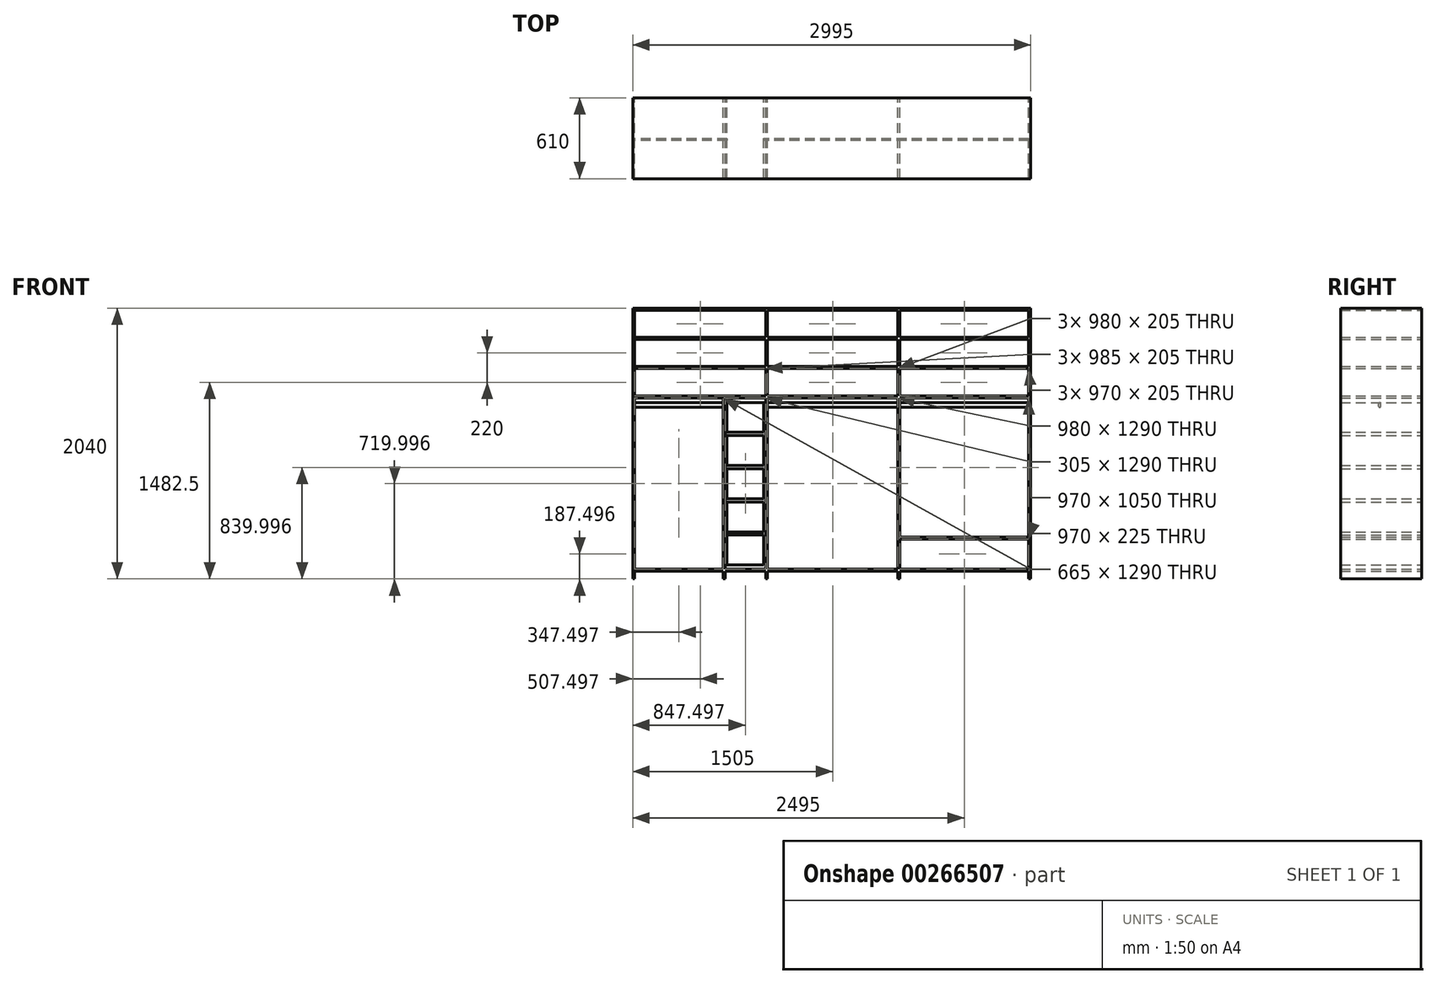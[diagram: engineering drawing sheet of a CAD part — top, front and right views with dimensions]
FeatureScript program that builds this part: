
annotation { "Feature Type Name" : "Feature", "Feature Type Description" : "" }
export const myFeature = defineFeature(function(context is Context, id is Id, definition is map)
    precondition{}
    {
        {
            var Q0;
            Q0=qCreatedBy(makeId("Front.planeOp"),FACE);
            var sketch = newSketch(context, id + "F0", { "sketchPlane" : qUnion([Q0])});
            skLineSegment(sketch, "E0.bottom", {"start": v(253.93, 1797.17) * mm, "end": v(268.93, 1797.17) * mm});
            skLineSegment(sketch, "E0.top", {"start": v(253.93, -242.83) * mm, "end": v(268.93, -242.83) * mm});
            skLineSegment(sketch, "E0.left", {"start": v(253.93, 1797.17) * mm, "end": v(253.93, -242.83) * mm});
            skLineSegment(sketch, "E0.right", {"start": v(268.93, 1797.17) * mm, "end": v(268.93, -242.83) * mm});
            skLineSegment(sketch, "E1.bottom", {"start": v(268.93, -182.83) * mm, "end": v(933.93, -182.83) * mm});
            skLineSegment(sketch, "E1.top", {"start": v(268.93, -167.83) * mm, "end": v(933.93, -167.83) * mm});
            skLineSegment(sketch, "E1.left", {"start": v(268.93, -182.83) * mm, "end": v(268.93, -167.83) * mm});
            skLineSegment(sketch, "E1.right", {"start": v(933.93, -182.83) * mm, "end": v(933.93, -167.83) * mm});
            skLineSegment(sketch, "E2.bottom", {"start": v(1268.93, -242.83) * mm, "end": v(1253.93, -242.83) * mm});
            skLineSegment(sketch, "E2.top", {"start": v(1268.93, 1797.17) * mm, "end": v(1253.93, 1797.17) * mm});
            skLineSegment(sketch, "E2.left", {"start": v(1268.93, -242.83) * mm, "end": v(1268.93, 1797.17) * mm});
            skLineSegment(sketch, "E2.right", {"start": v(1253.93, -242.83) * mm, "end": v(1253.93, 1797.17) * mm});
            skLineSegment(sketch, "E3.bottom", {"start": v(268.93, 1797.17) * mm, "end": v(1253.93, 1797.17) * mm});
            skLineSegment(sketch, "E3.top", {"start": v(268.93, 1782.17) * mm, "end": v(1253.93, 1782.17) * mm});
            skLineSegment(sketch, "E3.left", {"start": v(268.93, 1797.17) * mm, "end": v(268.93, 1782.17) * mm});
            skLineSegment(sketch, "E3.right", {"start": v(1253.93, 1797.17) * mm, "end": v(1253.93, 1782.17) * mm});
            skLineSegment(sketch, "E4.bottom", {"start": v(268.93, 1577.17) * mm, "end": v(1253.93, 1577.17) * mm});
            skLineSegment(sketch, "E4.top", {"start": v(268.93, 1562.17) * mm, "end": v(1253.93, 1562.17) * mm});
            skLineSegment(sketch, "E4.left", {"start": v(268.93, 1577.17) * mm, "end": v(268.93, 1562.17) * mm});
            skLineSegment(sketch, "E4.right", {"start": v(1253.93, 1577.17) * mm, "end": v(1253.93, 1562.17) * mm});
            skLineSegment(sketch, "E5.bottom", {"start": v(268.93, 1357.17) * mm, "end": v(1253.93, 1357.17) * mm});
            skLineSegment(sketch, "E5.top", {"start": v(268.93, 1342.17) * mm, "end": v(1253.93, 1342.17) * mm});
            skLineSegment(sketch, "E5.left", {"start": v(268.93, 1357.17) * mm, "end": v(268.93, 1342.17) * mm});
            skLineSegment(sketch, "E5.right", {"start": v(1253.93, 1357.17) * mm, "end": v(1253.93, 1342.17) * mm});
            skLineSegment(sketch, "E6.bottom", {"start": v(268.93, 1137.17) * mm, "end": v(1253.93, 1137.17) * mm});
            skLineSegment(sketch, "E6.top", {"start": v(268.93, 1122.17) * mm, "end": v(1253.93, 1122.17) * mm});
            skLineSegment(sketch, "E6.left", {"start": v(268.93, 1137.17) * mm, "end": v(268.93, 1122.17) * mm});
            skLineSegment(sketch, "E6.right", {"start": v(1253.93, 1137.17) * mm, "end": v(1253.93, 1122.17) * mm});
            skLineSegment(sketch, "E7.bottom", {"start": v(933.93, -242.83) * mm, "end": v(948.93, -242.83) * mm});
            skLineSegment(sketch, "E7.top", {"start": v(933.93, 1122.17) * mm, "end": v(948.93, 1122.17) * mm});
            skLineSegment(sketch, "E7.left", {"start": v(933.93, -242.83) * mm, "end": v(933.93, 1122.17) * mm});
            skLineSegment(sketch, "E7.right", {"start": v(948.93, -242.83) * mm, "end": v(948.93, 1122.17) * mm});
            skLineSegment(sketch, "E8.bottom", {"start": v(948.93, -167.83) * mm, "end": v(1253.93, -167.83) * mm});
            skLineSegment(sketch, "E8.top", {"start": v(948.93, -182.83) * mm, "end": v(1253.93, -182.83) * mm});
            skLineSegment(sketch, "E8.left", {"start": v(948.93, -167.83) * mm, "end": v(948.93, -182.83) * mm});
            skLineSegment(sketch, "E8.right", {"start": v(1253.93, -167.83) * mm, "end": v(1253.93, -182.83) * mm});
            skLineSegment(sketch, "E9.bottom", {"start": v(1238.93, 862.17) * mm, "end": v(963.93, 862.17) * mm});
            skLineSegment(sketch, "E9.top", {"start": v(1238.93, 1087.17) * mm, "end": v(963.93, 1087.17) * mm});
            skLineSegment(sketch, "E9.left", {"start": v(1238.93, 862.17) * mm, "end": v(1238.93, 1087.17) * mm});
            skLineSegment(sketch, "E9.right", {"start": v(963.93, 862.17) * mm, "end": v(963.93, 1087.17) * mm});
            skLineSegment(sketch, "E10", {"start": v(963.93, 862.17) * mm, "end": v(963.93, 660.08) * mm, "construction": true});
            skLineSegment(sketch, "E11.1.0.0", {"start": v(1238.93, 612.17) * mm, "end": v(1238.93, 837.17) * mm});
            skLineSegment(sketch, "E11.1.0.1", {"start": v(963.93, 612.17) * mm, "end": v(963.93, 837.17) * mm});
            skLineSegment(sketch, "E11.1.0.2", {"start": v(1238.93, 612.17) * mm, "end": v(963.93, 612.17) * mm});
            skLineSegment(sketch, "E11.1.0.3", {"start": v(1238.93, 837.17) * mm, "end": v(963.93, 837.17) * mm});
            skLineSegment(sketch, "E11.2.0.0", {"start": v(1238.93, 362.17) * mm, "end": v(1238.93, 587.17) * mm});
            skLineSegment(sketch, "E11.2.0.1", {"start": v(963.93, 362.17) * mm, "end": v(963.93, 587.17) * mm});
            skLineSegment(sketch, "E11.2.0.2", {"start": v(1238.93, 362.17) * mm, "end": v(963.93, 362.17) * mm});
            skLineSegment(sketch, "E11.2.0.3", {"start": v(1238.93, 587.17) * mm, "end": v(963.93, 587.17) * mm});
            skLineSegment(sketch, "E11.direction1", {"start": v(963.93, 862.17) * mm, "end": v(963.93, 612.17) * mm, "construction": true});
            skLineSegment(sketch, "E12.0.3.0", {"start": v(1238.93, 112.17) * mm, "end": v(1238.93, 337.17) * mm});
            skLineSegment(sketch, "E12.3.3.0", {"start": v(963.93, 112.17) * mm, "end": v(963.93, 337.17) * mm});
            skLineSegment(sketch, "E12.6.3.0", {"start": v(1238.93, 112.17) * mm, "end": v(963.93, 112.17) * mm});
            skLineSegment(sketch, "E12.9.3.0", {"start": v(1238.93, 337.17) * mm, "end": v(963.93, 337.17) * mm});
            skLineSegment(sketch, "E12.0.4.0", {"start": v(1238.93, -137.83) * mm, "end": v(1238.93, 87.17) * mm});
            skLineSegment(sketch, "E12.3.4.0", {"start": v(963.93, -137.83) * mm, "end": v(963.93, 87.17) * mm});
            skLineSegment(sketch, "E12.6.4.0", {"start": v(1238.93, -137.83) * mm, "end": v(963.93, -137.83) * mm});
            skLineSegment(sketch, "E12.9.4.0", {"start": v(1238.93, 87.17) * mm, "end": v(963.93, 87.17) * mm});
            skLineSegment(sketch, "E13.bottom", {"start": v(2248.93, 1797.17) * mm, "end": v(2263.93, 1797.17) * mm});
            skLineSegment(sketch, "E13.top", {"start": v(2248.93, -242.83) * mm, "end": v(2263.93, -242.83) * mm});
            skLineSegment(sketch, "E13.left", {"start": v(2248.93, 1797.17) * mm, "end": v(2248.93, -242.83) * mm});
            skLineSegment(sketch, "E13.right", {"start": v(2263.93, 1797.17) * mm, "end": v(2263.93, -242.83) * mm});
            skLineSegment(sketch, "E14.bottom", {"start": v(1268.93, -167.83) * mm, "end": v(2248.93, -167.83) * mm});
            skLineSegment(sketch, "E14.top", {"start": v(1268.93, -182.83) * mm, "end": v(2248.93, -182.83) * mm});
            skLineSegment(sketch, "E14.left", {"start": v(1268.93, -167.83) * mm, "end": v(1268.93, -182.83) * mm});
            skLineSegment(sketch, "E14.right", {"start": v(2248.93, -167.83) * mm, "end": v(2248.93, -182.83) * mm});
            skLineSegment(sketch, "E15.bottom", {"start": v(1268.93, 1122.17) * mm, "end": v(2248.93, 1122.17) * mm});
            skLineSegment(sketch, "E15.top", {"start": v(1268.93, 1137.17) * mm, "end": v(2248.93, 1137.17) * mm});
            skLineSegment(sketch, "E15.left", {"start": v(1268.93, 1122.17) * mm, "end": v(1268.93, 1137.17) * mm});
            skLineSegment(sketch, "E15.right", {"start": v(2248.93, 1122.17) * mm, "end": v(2248.93, 1137.17) * mm});
            skLineSegment(sketch, "E16.bottom", {"start": v(1268.93, 1342.17) * mm, "end": v(2248.93, 1342.17) * mm});
            skLineSegment(sketch, "E16.top", {"start": v(1268.93, 1357.17) * mm, "end": v(2248.93, 1357.17) * mm});
            skLineSegment(sketch, "E16.left", {"start": v(1268.93, 1342.17) * mm, "end": v(1268.93, 1357.17) * mm});
            skLineSegment(sketch, "E16.right", {"start": v(2248.93, 1342.17) * mm, "end": v(2248.93, 1357.17) * mm});
            skLineSegment(sketch, "E17.bottom", {"start": v(1268.93, 1562.17) * mm, "end": v(2248.93, 1562.17) * mm});
            skLineSegment(sketch, "E17.top", {"start": v(1268.93, 1577.17) * mm, "end": v(2248.93, 1577.17) * mm});
            skLineSegment(sketch, "E17.left", {"start": v(1268.93, 1562.17) * mm, "end": v(1268.93, 1577.17) * mm});
            skLineSegment(sketch, "E17.right", {"start": v(2248.93, 1562.17) * mm, "end": v(2248.93, 1577.17) * mm});
            skLineSegment(sketch, "E18.bottom", {"start": v(1268.93, 1782.17) * mm, "end": v(2248.93, 1782.17) * mm});
            skLineSegment(sketch, "E18.top", {"start": v(1268.93, 1797.17) * mm, "end": v(2248.93, 1797.17) * mm});
            skLineSegment(sketch, "E18.left", {"start": v(1268.93, 1782.17) * mm, "end": v(1268.93, 1797.17) * mm});
            skLineSegment(sketch, "E18.right", {"start": v(2248.93, 1782.17) * mm, "end": v(2248.93, 1797.17) * mm});
            skLineSegment(sketch, "E19.bottom", {"start": v(3233.93, 1797.17) * mm, "end": v(3248.93, 1797.17) * mm});
            skLineSegment(sketch, "E19.top", {"start": v(3233.93, -242.83) * mm, "end": v(3248.93, -242.83) * mm});
            skLineSegment(sketch, "E19.left", {"start": v(3233.93, 1797.17) * mm, "end": v(3233.93, -242.83) * mm});
            skLineSegment(sketch, "E19.right", {"start": v(3248.93, 1797.17) * mm, "end": v(3248.93, -242.83) * mm});
            skLineSegment(sketch, "E20.bottom", {"start": v(2263.93, 1782.17) * mm, "end": v(3233.93, 1782.17) * mm});
            skLineSegment(sketch, "E20.top", {"start": v(2263.93, 1797.17) * mm, "end": v(3233.93, 1797.17) * mm});
            skLineSegment(sketch, "E20.left", {"start": v(2263.93, 1782.17) * mm, "end": v(2263.93, 1797.17) * mm});
            skLineSegment(sketch, "E20.right", {"start": v(3233.93, 1782.17) * mm, "end": v(3233.93, 1797.17) * mm});
            skLineSegment(sketch, "E21.bottom", {"start": v(2263.93, 1562.17) * mm, "end": v(3233.93, 1562.17) * mm});
            skLineSegment(sketch, "E21.top", {"start": v(2263.93, 1577.17) * mm, "end": v(3233.93, 1577.17) * mm});
            skLineSegment(sketch, "E21.left", {"start": v(2263.93, 1562.17) * mm, "end": v(2263.93, 1577.17) * mm});
            skLineSegment(sketch, "E21.right", {"start": v(3233.93, 1562.17) * mm, "end": v(3233.93, 1577.17) * mm});
            skLineSegment(sketch, "E22.bottom", {"start": v(2263.93, 1357.17) * mm, "end": v(3233.93, 1357.17) * mm});
            skLineSegment(sketch, "E22.top", {"start": v(2263.93, 1342.17) * mm, "end": v(3233.93, 1342.17) * mm});
            skLineSegment(sketch, "E22.left", {"start": v(2263.93, 1357.17) * mm, "end": v(2263.93, 1342.17) * mm});
            skLineSegment(sketch, "E22.right", {"start": v(3233.93, 1357.17) * mm, "end": v(3233.93, 1342.17) * mm});
            skLineSegment(sketch, "E23.bottom", {"start": v(2263.93, 1137.17) * mm, "end": v(3233.93, 1137.17) * mm});
            skLineSegment(sketch, "E23.top", {"start": v(2263.93, 1122.17) * mm, "end": v(3233.93, 1122.17) * mm});
            skLineSegment(sketch, "E23.left", {"start": v(2263.93, 1137.17) * mm, "end": v(2263.93, 1122.17) * mm});
            skLineSegment(sketch, "E23.right", {"start": v(3233.93, 1137.17) * mm, "end": v(3233.93, 1122.17) * mm});
            skLineSegment(sketch, "E24.bottom", {"start": v(2263.93, -167.83) * mm, "end": v(3233.93, -167.83) * mm});
            skLineSegment(sketch, "E24.top", {"start": v(2263.93, -182.83) * mm, "end": v(3233.93, -182.83) * mm});
            skLineSegment(sketch, "E24.left", {"start": v(2263.93, -167.83) * mm, "end": v(2263.93, -182.83) * mm});
            skLineSegment(sketch, "E24.right", {"start": v(3233.93, -167.83) * mm, "end": v(3233.93, -182.83) * mm});
            skLineSegment(sketch, "E25.bottom", {"start": v(2263.93, 57.17) * mm, "end": v(3233.93, 57.17) * mm});
            skLineSegment(sketch, "E25.top", {"start": v(2263.93, 72.17) * mm, "end": v(3233.93, 72.17) * mm});
            skLineSegment(sketch, "E25.left", {"start": v(2263.93, 57.17) * mm, "end": v(2263.93, 72.17) * mm});
            skLineSegment(sketch, "E25.right", {"start": v(3233.93, 57.17) * mm, "end": v(3233.93, 72.17) * mm});
            skSolve(sketch);
        }
        {
            var Q0;
            {var subQ4=sQuery(id+"F0.wireOp",EDGE,"E2.bottom");Q0=makeQuery(id+"F0.imprint","IMPRINT",FACE,{"disambiguationData":[TD([[makeQuery(id+"F0.imprint","IMPRINT",EDGE,{"derivedFrom":subQ4}),-1.0]])]});}
            var Q1;
            Q1=makeQuery(id+"F0.imprint","IMPRINT",FACE,{"disambiguationData":[TD([[makeQuery(id+"F0.imprint","IMPRINT",EDGE,{"derivedFrom":sQuery(id+"F0.wireOp",EDGE,"E0.bottom")}),-1.0]])]});
            var Q2;
            {var subQ3=sQuery(id+"F0.wireOp",EDGE,"E7.bottom");Q2=makeQuery(id+"F0.imprint","IMPRINT",FACE,{"disambiguationData":[TD([[makeQuery(id+"F0.imprint","IMPRINT",EDGE,{"derivedFrom":subQ3}),1.0]])]});}
            var Q3;
            Q3=makeQuery(id+"F0.imprint","IMPRINT",FACE,{"disambiguationData":[TD([[makeQuery(id+"F0.imprint","IMPRINT",EDGE,{"derivedFrom":sQuery(id+"F0.wireOp",EDGE,"E3.bottom")}),-1.0]])]});
            var Q4;
            Q4=makeQuery(id+"F0.imprint","IMPRINT",FACE,{"disambiguationData":[TD([[makeQuery(id+"F0.imprint","IMPRINT",EDGE,{"derivedFrom":sQuery(id+"F0.wireOp",EDGE,"E4.bottom")}),-1.0]])]});
            var Q5;
            Q5=makeQuery(id+"F0.imprint","IMPRINT",FACE,{"disambiguationData":[TD([[makeQuery(id+"F0.imprint","IMPRINT",EDGE,{"derivedFrom":sQuery(id+"F0.wireOp",EDGE,"E5.bottom")}),-1.0]])]});
            var Q6;
            Q6=makeQuery(id+"F0.imprint","IMPRINT",FACE,{"disambiguationData":[TD([[makeQuery(id+"F0.imprint","IMPRINT",EDGE,{"derivedFrom":sQuery(id+"F0.wireOp",EDGE,"E6.bottom")}),-1.0]])]});
            var Q7;
            {var subQ0=sQuery(id+"F0.wireOp",EDGE,"E1.bottom");Q7=makeQuery(id+"F0.imprint","IMPRINT",FACE,{"disambiguationData":[TD([[makeQuery(id+"F0.imprint","IMPRINT",EDGE,{"derivedFrom":subQ0}),1.0]])]});}
            var Q8;
            Q8=makeQuery(id+"F0.imprint","IMPRINT",FACE,{"disambiguationData":[TD([[makeQuery(id+"F0.imprint","IMPRINT",EDGE,{"derivedFrom":sQuery(id+"F0.wireOp",EDGE,"E8.bottom")}),-1.0]])]});
            var Q9;
            Q9=makeQuery(id+"F0.imprint","IMPRINT",FACE,{"disambiguationData":[TD([[makeQuery(id+"F0.imprint","IMPRINT",EDGE,{"derivedFrom":sQuery(id+"F0.wireOp",EDGE,"E18.bottom")}),1.0]])]});
            var Q10;
            Q10=makeQuery(id+"F0.imprint","IMPRINT",FACE,{"disambiguationData":[TD([[makeQuery(id+"F0.imprint","IMPRINT",EDGE,{"derivedFrom":sQuery(id+"F0.wireOp",EDGE,"E20.bottom")}),1.0]])]});
            var Q11;
            Q11=makeQuery(id+"F0.imprint","IMPRINT",FACE,{"disambiguationData":[TD([[makeQuery(id+"F0.imprint","IMPRINT",EDGE,{"derivedFrom":sQuery(id+"F0.wireOp",EDGE,"E17.bottom")}),1.0]])]});
            var Q12;
            Q12=makeQuery(id+"F0.imprint","IMPRINT",FACE,{"disambiguationData":[TD([[makeQuery(id+"F0.imprint","IMPRINT",EDGE,{"derivedFrom":sQuery(id+"F0.wireOp",EDGE,"E21.bottom")}),1.0]])]});
            var Q13;
            Q13=makeQuery(id+"F0.imprint","IMPRINT",FACE,{"disambiguationData":[TD([[makeQuery(id+"F0.imprint","IMPRINT",EDGE,{"derivedFrom":sQuery(id+"F0.wireOp",EDGE,"E22.bottom")}),-1.0]])]});
            var Q14;
            Q14=makeQuery(id+"F0.imprint","IMPRINT",FACE,{"disambiguationData":[TD([[makeQuery(id+"F0.imprint","IMPRINT",EDGE,{"derivedFrom":sQuery(id+"F0.wireOp",EDGE,"E16.bottom")}),1.0]])]});
            var Q15;
            Q15=makeQuery(id+"F0.imprint","IMPRINT",FACE,{"disambiguationData":[TD([[makeQuery(id+"F0.imprint","IMPRINT",EDGE,{"derivedFrom":sQuery(id+"F0.wireOp",EDGE,"E15.bottom")}),1.0]])]});
            var Q16;
            Q16=makeQuery(id+"F0.imprint","IMPRINT",FACE,{"disambiguationData":[TD([[makeQuery(id+"F0.imprint","IMPRINT",EDGE,{"derivedFrom":sQuery(id+"F0.wireOp",EDGE,"E23.bottom")}),-1.0]])]});
            var Q17;
            Q17=makeQuery(id+"F0.imprint","IMPRINT",FACE,{"disambiguationData":[TD([[makeQuery(id+"F0.imprint","IMPRINT",EDGE,{"derivedFrom":sQuery(id+"F0.wireOp",EDGE,"E13.bottom")}),-1.0]])]});
            var Q18;
            Q18=makeQuery(id+"F0.imprint","IMPRINT",FACE,{"disambiguationData":[TD([[makeQuery(id+"F0.imprint","IMPRINT",EDGE,{"derivedFrom":sQuery(id+"F0.wireOp",EDGE,"E19.bottom")}),-1.0]])]});
            var Q19;
            Q19=makeQuery(id+"F0.imprint","IMPRINT",FACE,{"disambiguationData":[TD([[makeQuery(id+"F0.imprint","IMPRINT",EDGE,{"derivedFrom":sQuery(id+"F0.wireOp",EDGE,"E24.bottom")}),-1.0]])]});
            var Q20;
            Q20=makeQuery(id+"F0.imprint","IMPRINT",FACE,{"disambiguationData":[TD([[makeQuery(id+"F0.imprint","IMPRINT",EDGE,{"derivedFrom":sQuery(id+"F0.wireOp",EDGE,"E14.bottom")}),-1.0]])]});
            var Q21;
            Q21=makeQuery(id+"F0.imprint","IMPRINT",FACE,{"disambiguationData":[TD([[makeQuery(id+"F0.imprint","IMPRINT",EDGE,{"derivedFrom":sQuery(id+"F0.wireOp",EDGE,"E25.bottom")}),1.0]])]});
            extrude(context, id + "F1", {"entities" : qUnion([Q0, Q1, Q2, Q3, Q4, Q5, Q6, Q7, Q8, Q9, Q10, Q11, Q12, Q13, Q14, Q15, Q16, Q17, Q18, Q19, Q20, Q21]), "depth" : 610 * mm});
        }
        {
            var Q0;
            {var subQ0=sQuery(id+"F0.wireOp",EDGE,"E0.right");Q0=makeQuery(id+"F1.opExtrude","SWEPT_FACE",FACE,{"disambiguationData":[OSD([subQ0]),TDD([makeQuery(id+"F0.imprint","IMPRINT",EDGE,{"disambiguationData":[TD([[makeQuery(id+"F0.imprint","INTERSECT",VERTEX,{"derivedFrom":[subQ0,sQuery(id+"F0.wireOp",EDGE,"E1.top"),sQuery(id+"F0.wireOp",EDGE,"E1.left")]}),1.0]])],"derivedFrom":subQ0})])]});}
            var sketch = newSketch(context, id + "F2", { "sketchPlane" : qUnion([Q0])});
            skPoint(sketch, "E26", {"position": v(-315, 1077.17) * mm});
            skLineSegment(sketch, "E27", {"start": v(-315, 1077.17) * mm, "end": v(-315, 1057.17) * mm, "construction": true});
            skPoint(sketch, "E28", {"position": v(-315, 1057.17) * mm});
            skArc(sketch, "E29", {"start": v(-322.5, 1057.17) * mm, "mid": v(-315, 1049.67) * mm, "end": v(-307.5, 1057.17) * mm});
            skArc(sketch, "E30", {"start": v(-322.5, 1077.17) * mm, "mid": v(-315, 1084.67) * mm, "end": v(-307.5, 1077.17) * mm});
            skLineSegment(sketch, "E31", {"start": v(-307.5, 1077.17) * mm, "end": v(-307.5, 1057.17) * mm});
            skLineSegment(sketch, "E32", {"start": v(-322.5, 1077.17) * mm, "end": v(-322.5, 1057.17) * mm});
            skSolve(sketch);
        }
        {
            var Q0;
            Q0=makeQuery(id+"F2.imprint","IMPRINT",FACE,{"disambiguationData":[TD([[makeQuery(id+"F2.imprint","IMPRINT",EDGE,{"derivedFrom":sQuery(id+"F2.wireOp",EDGE,"E29")}),1.0]])]});
            var Q1;
            {var subQ0=sQuery(id+"F0.wireOp",EDGE,"E19.left");Q1=makeQuery(id+"F1.opExtrude","SWEPT_FACE",FACE,{"disambiguationData":[OSD([subQ0]),TDD([makeQuery(id+"F0.imprint","IMPRINT",EDGE,{"disambiguationData":[TD([[makeQuery(id+"F0.imprint","INTERSECT",VERTEX,{"derivedFrom":[subQ0,sQuery(id+"F0.wireOp",EDGE,"E23.top"),sQuery(id+"F0.wireOp",EDGE,"E23.right")]}),-1.0]])],"derivedFrom":subQ0})])]});}
            extrude(context, id + "F3", {"entities" : qUnion([Q0]), "endBound" : BoundingType.UP_TO_SURFACE, "endBoundEntityFace" : qUnion([Q1]), "depth" : 25 * mm});
        }
        {
            var Q0;
            Q0=makeQuery(id+"F0.imprint","IMPRINT",FACE,{"disambiguationData":[TD([[makeQuery(id+"F0.imprint","IMPRINT",EDGE,{"derivedFrom":sQuery(id+"F0.wireOp",EDGE,"E9.bottom")}),-1.0]])]});
            var Q1;
            Q1=makeQuery(id+"F0.imprint","IMPRINT",FACE,{"disambiguationData":[TD([[makeQuery(id+"F0.imprint","IMPRINT",EDGE,{"derivedFrom":sQuery(id+"F0.wireOp",EDGE,"E11.1.0.0")}),1.0]])]});
            var Q2;
            Q2=makeQuery(id+"F0.imprint","IMPRINT",FACE,{"disambiguationData":[TD([[makeQuery(id+"F0.imprint","IMPRINT",EDGE,{"derivedFrom":sQuery(id+"F0.wireOp",EDGE,"E11.2.0.0")}),1.0]])]});
            var Q3;
            Q3=makeQuery(id+"F0.imprint","IMPRINT",FACE,{"disambiguationData":[TD([[makeQuery(id+"F0.imprint","IMPRINT",EDGE,{"derivedFrom":sQuery(id+"F0.wireOp",EDGE,"E12.0.3.0")}),1.0]])]});
            var Q4;
            Q4=makeQuery(id+"F0.imprint","IMPRINT",FACE,{"disambiguationData":[TD([[makeQuery(id+"F0.imprint","IMPRINT",EDGE,{"derivedFrom":sQuery(id+"F0.wireOp",EDGE,"E12.0.4.0")}),1.0]])]});
            extrude(context, id + "F4", {"entities" : qUnion([Q0, Q1, Q2, Q3, Q4]), "operationType" : NewBodyOperationType.ADD, "depth" : 610 * mm});
        }
    });
